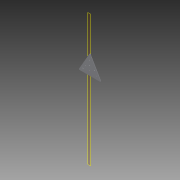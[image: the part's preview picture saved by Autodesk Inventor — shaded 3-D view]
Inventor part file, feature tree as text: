
AUTODESK INVENTOR PART (.ipt)
format: ipt  version: 2014 SP1 (Build 180222100, 222)  size: 99,328 bytes
history: native  units: in
note: dims shown in document units (in); Inventor stores cm internally (conversion verified against a paired STEP export)
features: reference x17, plane x1, extrude x1, fillet x1, sketch x1
ambient origin geometry x8: Origin, YZ Plane, XZ Plane, XY Plane, X Axis, Y Axis, Z Axis, Center Point
bodies: Solid1 (feature_tree)
feature tree (21):
  plane  "Work Plane1"
  extrude  "Extrusion1"  Depth=0.125in TaperAngle=0.0deg
  fillet  "Fillet1"  Radius=0.125in
  sketch  "Sketch1"  dims[d0=1.0in d1=0.125in d2=0.0in d3=0.125in]
  reference  "Reference1"
  reference  "Reference2"
  reference  "Reference3"
  reference  "Reference4"
  reference  "Reference5"
  reference  "Reference6"
  reference  "Reference7"
  reference  "Reference8"
  reference  "Reference9"
  reference  "Reference10"
  reference  "Reference11"
  reference  "Reference12"
  reference  "Reference13"
  reference  "Reference14"
  reference  "Reference15"
  reference  "Reference16"
  reference  "Reference17"
